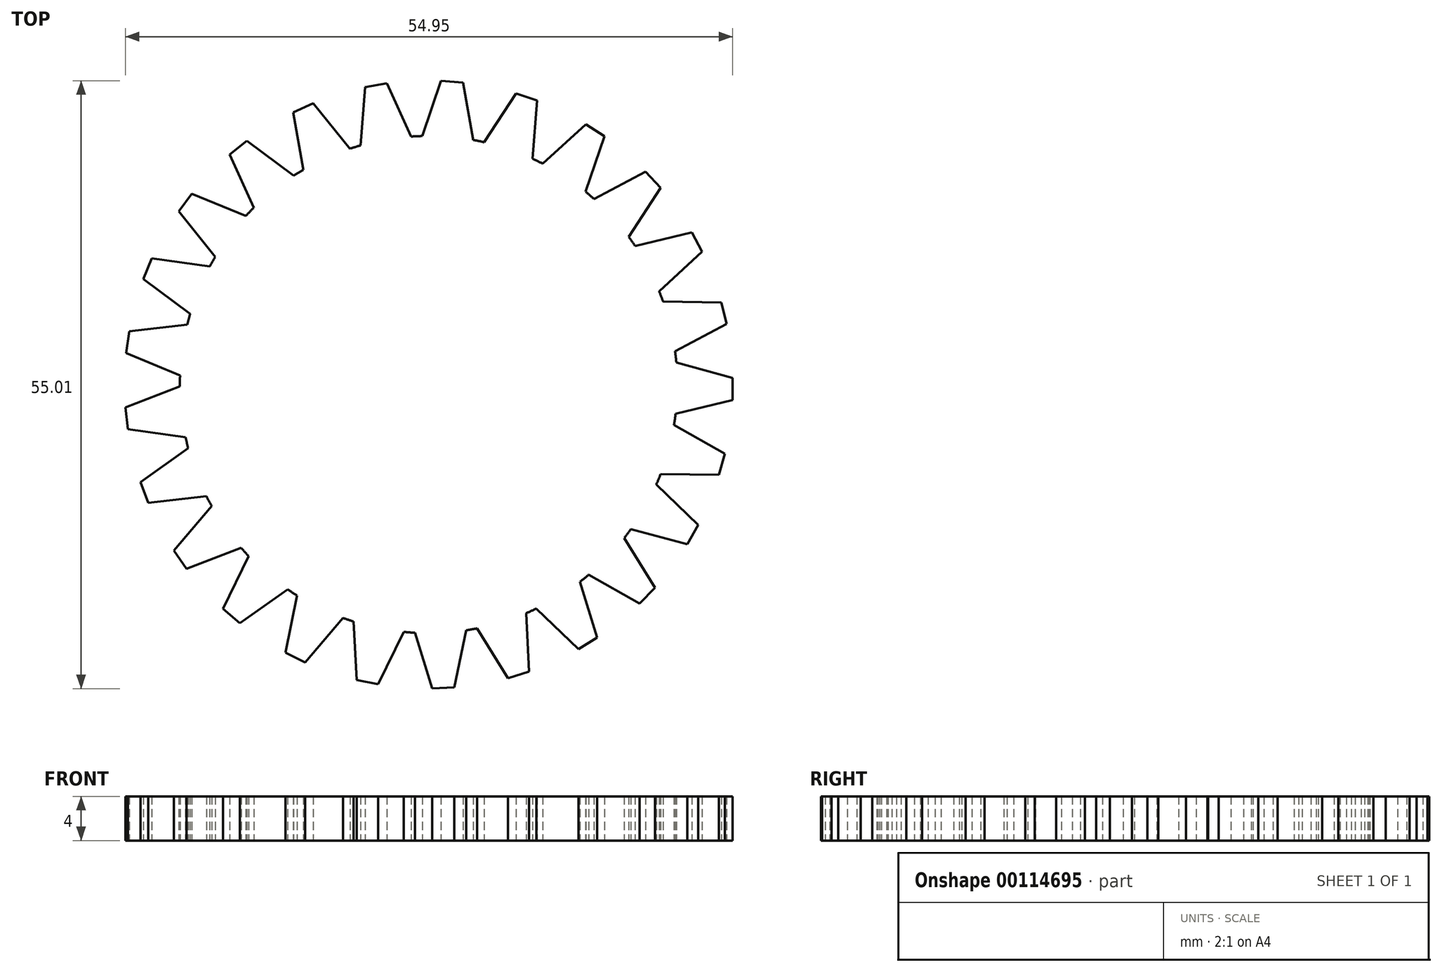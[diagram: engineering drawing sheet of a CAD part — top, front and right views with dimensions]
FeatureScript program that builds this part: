
annotation { "Feature Type Name" : "Feature", "Feature Type Description" : "" }
export const myFeature = defineFeature(function(context is Context, id is Id, definition is map)
    precondition{}
    {
        {
            var Q0;
            Q0=qCreatedBy(makeId("Top.planeOp"),FACE);
            var sketch = newSketch(context, id + "F0", { "sketchPlane" : qUnion([Q0])});
            skCircle(sketch, "E0", {"center": v(0, 0) * mm, "radius": 22.5 * mm});
            skLineSegment(sketch, "E1", {"start": v(-18, 13.49) * mm, "end": v(-22.02, 16.48) * mm});
            skLineSegment(sketch, "E2", {"start": v(-22.02, 16.48) * mm, "end": v(-21.42, 17.28) * mm});
            skLineSegment(sketch, "E3", {"start": v(-21.42, 17.28) * mm, "end": v(-16.52, 15.27) * mm});
            skLineSegment(sketch, "E4.MirrorCS", {"start": v(-22.61, 15.68) * mm, "end": v(-19.3, 11.56) * mm});
            skLineSegment(sketch, "E5.MirrorCS", {"start": v(-22.02, 16.48) * mm, "end": v(-22.61, 15.68) * mm});
            skLineSegment(sketch, "E6.1.0", {"start": v(-25.04, 11.41) * mm, "end": v(-19.8, 10.68) * mm});
            skLineSegment(sketch, "E6.1.1", {"start": v(-25.42, 10.49) * mm, "end": v(-25.8, 9.56) * mm});
            skLineSegment(sketch, "E6.1.2", {"start": v(-25.8, 9.56) * mm, "end": v(-21.57, 6.4) * mm});
            skLineSegment(sketch, "E6.1.3", {"start": v(-25.42, 10.49) * mm, "end": v(-25.04, 11.41) * mm});
            skLineSegment(sketch, "E6.2.0", {"start": v(-27.1, 4.82) * mm, "end": v(-21.84, 5.42) * mm});
            skLineSegment(sketch, "E6.2.1", {"start": v(-27.23, 3.83) * mm, "end": v(-27.37, 2.84) * mm});
            skLineSegment(sketch, "E6.2.2", {"start": v(-27.37, 2.84) * mm, "end": v(-22.48, 0.83) * mm});
            skLineSegment(sketch, "E6.2.3", {"start": v(-27.23, 3.83) * mm, "end": v(-27.1, 4.82) * mm});
            skLineSegment(sketch, "E7.1.3.0", {"start": v(-27.44, -2.06) * mm, "end": v(-22.5, -0.18) * mm});
            skLineSegment(sketch, "E7.3.3.0", {"start": v(-27.33, -3.06) * mm, "end": v(-27.22, -4.05) * mm});
            skLineSegment(sketch, "E7.6.3.0", {"start": v(-27.22, -4.05) * mm, "end": v(-21.98, -4.79) * mm});
            skLineSegment(sketch, "E7.9.3.0", {"start": v(-27.33, -3.06) * mm, "end": v(-27.44, -2.06) * mm});
            skLineSegment(sketch, "E7.1.4.0", {"start": v(-26.07, -8.82) * mm, "end": v(-21.75, -5.77) * mm});
            skLineSegment(sketch, "E7.3.4.0", {"start": v(-25.71, -9.76) * mm, "end": v(-25.35, -10.7) * mm});
            skLineSegment(sketch, "E7.6.4.0", {"start": v(-25.35, -10.7) * mm, "end": v(-20.1, -10.1) * mm});
            skLineSegment(sketch, "E7.9.4.0", {"start": v(-25.71, -9.76) * mm, "end": v(-26.07, -8.82) * mm});
            skLineSegment(sketch, "E7.1.5.0", {"start": v(-23.05, -15.03) * mm, "end": v(-19.63, -11) * mm});
            skLineSegment(sketch, "E7.3.5.0", {"start": v(-22.48, -15.85) * mm, "end": v(-21.9, -16.66) * mm});
            skLineSegment(sketch, "E7.6.5.0", {"start": v(-21.9, -16.66) * mm, "end": v(-16.95, -14.78) * mm});
            skLineSegment(sketch, "E7.9.5.0", {"start": v(-22.48, -15.85) * mm, "end": v(-23.05, -15.03) * mm});
            skLineSegment(sketch, "E7.1.6.0", {"start": v(-18.6, -20.3) * mm, "end": v(-16.28, -15.53) * mm});
            skLineSegment(sketch, "E7.3.6.0", {"start": v(-17.83, -20.94) * mm, "end": v(-17.07, -21.59) * mm});
            skLineSegment(sketch, "E7.6.6.0", {"start": v(-17.07, -21.59) * mm, "end": v(-12.74, -18.53) * mm});
            skLineSegment(sketch, "E7.9.6.0", {"start": v(-17.83, -20.94) * mm, "end": v(-18.6, -20.3) * mm});
            skLineSegment(sketch, "E7.1.7.0", {"start": v(-12.96, -24.28) * mm, "end": v(-11.9, -19.1) * mm});
            skLineSegment(sketch, "E7.3.7.0", {"start": v(-12.06, -24.71) * mm, "end": v(-11.16, -25.15) * mm});
            skLineSegment(sketch, "E7.6.7.0", {"start": v(-11.16, -25.15) * mm, "end": v(-7.74, -21.12) * mm});
            skLineSegment(sketch, "E7.9.7.0", {"start": v(-12.06, -24.71) * mm, "end": v(-12.96, -24.28) * mm});
            skLineSegment(sketch, "E7.1.8.0", {"start": v(-6.52, -26.74) * mm, "end": v(-6.78, -21.45) * mm});
            skLineSegment(sketch, "E7.3.8.0", {"start": v(-5.54, -26.94) * mm, "end": v(-4.56, -27.14) * mm});
            skLineSegment(sketch, "E7.6.8.0", {"start": v(-4.56, -27.14) * mm, "end": v(-2.24, -22.38) * mm});
            skLineSegment(sketch, "E7.9.8.0", {"start": v(-5.54, -26.94) * mm, "end": v(-6.52, -26.74) * mm});
            skLineSegment(sketch, "E7.1.9.0", {"start": v(0.34, -27.52) * mm, "end": v(-1.23, -22.47) * mm});
            skLineSegment(sketch, "E7.3.9.0", {"start": v(1.34, -27.47) * mm, "end": v(2.33, -27.42) * mm});
            skLineSegment(sketch, "E7.6.9.0", {"start": v(2.33, -27.42) * mm, "end": v(3.4, -22.24) * mm});
            skLineSegment(sketch, "E7.9.9.0", {"start": v(1.34, -27.47) * mm, "end": v(0.34, -27.52) * mm});
            skLineSegment(sketch, "E7.1.10.0", {"start": v(7.17, -26.57) * mm, "end": v(4.4, -22.07) * mm});
            skLineSegment(sketch, "E7.3.10.0", {"start": v(8.13, -26.27) * mm, "end": v(9.08, -25.98) * mm});
            skLineSegment(sketch, "E7.6.10.0", {"start": v(9.08, -25.98) * mm, "end": v(8.82, -20.7) * mm});
            skLineSegment(sketch, "E7.9.10.0", {"start": v(8.13, -26.27) * mm, "end": v(7.17, -26.57) * mm});
            skLineSegment(sketch, "E7.1.11.0", {"start": v(13.55, -23.95) * mm, "end": v(9.74, -20.28) * mm});
            skLineSegment(sketch, "E7.3.11.0", {"start": v(14.4, -23.43) * mm, "end": v(15.25, -22.9) * mm});
            skLineSegment(sketch, "E7.6.11.0", {"start": v(15.25, -22.9) * mm, "end": v(13.69, -17.85) * mm});
            skLineSegment(sketch, "E7.9.11.0", {"start": v(14.4, -23.43) * mm, "end": v(13.55, -23.95) * mm});
            skLineSegment(sketch, "E7.1.12.0", {"start": v(19.08, -19.83) * mm, "end": v(14.48, -17.22) * mm});
            skLineSegment(sketch, "E7.3.12.0", {"start": v(19.78, -19.1) * mm, "end": v(20.47, -18.39) * mm});
            skLineSegment(sketch, "E7.6.12.0", {"start": v(20.47, -18.39) * mm, "end": v(17.7, -13.88) * mm});
            skLineSegment(sketch, "E7.9.12.0", {"start": v(19.78, -19.1) * mm, "end": v(19.08, -19.83) * mm});
            skLineSegment(sketch, "E7.1.13.0", {"start": v(23.41, -14.46) * mm, "end": v(18.3, -13.08) * mm});
            skLineSegment(sketch, "E7.3.13.0", {"start": v(23.9, -13.59) * mm, "end": v(24.4, -12.72) * mm});
            skLineSegment(sketch, "E7.6.13.0", {"start": v(24.4, -12.72) * mm, "end": v(20.6, -9.05) * mm});
            skLineSegment(sketch, "E7.9.13.0", {"start": v(23.9, -13.59) * mm, "end": v(23.41, -14.46) * mm});
            skLineSegment(sketch, "E7.1.14.0", {"start": v(26.27, -8.18) * mm, "end": v(20.99, -8.12) * mm});
            skLineSegment(sketch, "E7.3.14.0", {"start": v(26.54, -7.22) * mm, "end": v(26.8, -6.25) * mm});
            skLineSegment(sketch, "E7.6.14.0", {"start": v(26.8, -6.25) * mm, "end": v(22.2, -3.64) * mm});
            skLineSegment(sketch, "E7.9.14.0", {"start": v(26.54, -7.22) * mm, "end": v(26.27, -8.18) * mm});
            skLineSegment(sketch, "E7.1.15.0", {"start": v(27.48, -1.4) * mm, "end": v(22.34, -2.64) * mm});
            skLineSegment(sketch, "E7.3.15.0", {"start": v(27.5, -0.4) * mm, "end": v(27.51, 0.6) * mm});
            skLineSegment(sketch, "E7.6.15.0", {"start": v(27.51, 0.6) * mm, "end": v(22.4, 2) * mm});
            skLineSegment(sketch, "E7.9.15.0", {"start": v(27.5, -0.4) * mm, "end": v(27.48, -1.4) * mm});
            skLineSegment(sketch, "E7.1.16.0", {"start": v(26.97, 5.49) * mm, "end": v(22.3, 3) * mm});
            skLineSegment(sketch, "E7.3.16.0", {"start": v(26.73, 6.46) * mm, "end": v(26.5, 7.43) * mm});
            skLineSegment(sketch, "E7.6.16.0", {"start": v(26.5, 7.43) * mm, "end": v(21.2, 7.5) * mm});
            skLineSegment(sketch, "E7.9.16.0", {"start": v(26.73, 6.46) * mm, "end": v(26.97, 5.49) * mm});
            skLineSegment(sketch, "E7.1.17.0", {"start": v(24.75, 12.02) * mm, "end": v(20.85, 8.45) * mm});
            skLineSegment(sketch, "E7.3.17.0", {"start": v(24.28, 12.9) * mm, "end": v(23.81, 13.79) * mm});
            skLineSegment(sketch, "E7.6.17.0", {"start": v(23.81, 13.79) * mm, "end": v(18.67, 12.54) * mm});
            skLineSegment(sketch, "E7.9.17.0", {"start": v(24.28, 12.9) * mm, "end": v(24.75, 12.02) * mm});
            skLineSegment(sketch, "E7.1.18.0", {"start": v(20.99, 17.8) * mm, "end": v(18.1, 13.37) * mm});
            skLineSegment(sketch, "E7.3.18.0", {"start": v(20.31, 18.54) * mm, "end": v(19.64, 19.28) * mm});
            skLineSegment(sketch, "E7.6.18.0", {"start": v(19.64, 19.28) * mm, "end": v(14.97, 16.8) * mm});
            skLineSegment(sketch, "E7.9.18.0", {"start": v(20.31, 18.54) * mm, "end": v(20.99, 17.8) * mm});
            skLineSegment(sketch, "E7.1.19.0", {"start": v(15.9, 22.46) * mm, "end": v(14.2, 17.45) * mm});
            skLineSegment(sketch, "E7.3.19.0", {"start": v(15.06, 23) * mm, "end": v(14.23, 23.55) * mm});
            skLineSegment(sketch, "E7.6.19.0", {"start": v(14.23, 23.55) * mm, "end": v(10.32, 19.99) * mm});
            skLineSegment(sketch, "E7.9.19.0", {"start": v(15.06, 23) * mm, "end": v(15.9, 22.46) * mm});
            skLineSegment(sketch, "E7.1.20.0", {"start": v(9.82, 25.7) * mm, "end": v(9.42, 20.43) * mm});
            skLineSegment(sketch, "E7.3.20.0", {"start": v(8.87, 26.03) * mm, "end": v(7.92, 26.35) * mm});
            skLineSegment(sketch, "E7.6.20.0", {"start": v(7.92, 26.35) * mm, "end": v(5.03, 21.92) * mm});
            skLineSegment(sketch, "E7.9.20.0", {"start": v(8.87, 26.03) * mm, "end": v(9.82, 25.7) * mm});
            skLineSegment(sketch, "E7.1.21.0", {"start": v(3.11, 27.34) * mm, "end": v(4.04, 22.13) * mm});
            skLineSegment(sketch, "E7.3.21.0", {"start": v(2.12, 27.42) * mm, "end": v(1.12, 27.5) * mm});
            skLineSegment(sketch, "E7.6.21.0", {"start": v(1.12, 27.5) * mm, "end": v(-0.58, 22.49) * mm});
            skLineSegment(sketch, "E7.9.21.0", {"start": v(2.12, 27.42) * mm, "end": v(3.11, 27.34) * mm});
            skLineSegment(sketch, "E7.1.22.0", {"start": v(-3.78, 27.26) * mm, "end": v(-1.6, 22.44) * mm});
            skLineSegment(sketch, "E7.3.22.0", {"start": v(-4.77, 27.08) * mm, "end": v(-5.75, 26.9) * mm});
            skLineSegment(sketch, "E7.6.22.0", {"start": v(-5.75, 26.9) * mm, "end": v(-6.16, 21.63) * mm});
            skLineSegment(sketch, "E7.9.22.0", {"start": v(-4.77, 27.08) * mm, "end": v(-3.78, 27.26) * mm});
            skLineSegment(sketch, "E7.1.23.0", {"start": v(-10.44, 25.46) * mm, "end": v(-7.12, 21.34) * mm});
            skLineSegment(sketch, "E7.3.23.0", {"start": v(-11.35, 25.05) * mm, "end": v(-12.26, 24.63) * mm});
            skLineSegment(sketch, "E7.6.23.0", {"start": v(-12.26, 24.63) * mm, "end": v(-11.34, 19.42) * mm});
            skLineSegment(sketch, "E7.9.23.0", {"start": v(-11.35, 25.05) * mm, "end": v(-10.44, 25.46) * mm});
            skLineSegment(sketch, "E7.1.24.0", {"start": v(-16.45, 22.06) * mm, "end": v(-12.2, 18.9) * mm});
            skLineSegment(sketch, "E7.3.24.0", {"start": v(-17.23, 21.44) * mm, "end": v(-18, 20.8) * mm});
            skLineSegment(sketch, "E7.6.24.0", {"start": v(-18, 20.8) * mm, "end": v(-15.82, 16) * mm});
            skLineSegment(sketch, "E7.9.24.0", {"start": v(-17.23, 21.44) * mm, "end": v(-16.45, 22.06) * mm});
            skSolve(sketch);
        }
        {
            var Q0;
            Q0 = qSketchRegion(id + "F0", true);
            var Q1;
            {var subQ0=sQuery(id+"F0.wireOp",EDGE,"E0");var subQ35=makeQuery(id+"F0.imprint","INTERSECT",VERTEX,{"derivedFrom":[subQ0,sQuery(id+"F0.wireOp",EDGE,"E7.1.25.0")]});Q1=makeQuery(id+"F0.imprint","IMPRINT",FACE,{"disambiguationData":[TD([[makeQuery(id+"F0.imprint","IMPRINT",EDGE,{"disambiguationData":[TD([[subQ35,-1.0]])],"derivedFrom":subQ0}),1.0]])]});}
            extrude(context, id + "F1", {"entities" : qUnion([Q0, Q1]), "depth" : 4 * mm});
        }
    });
